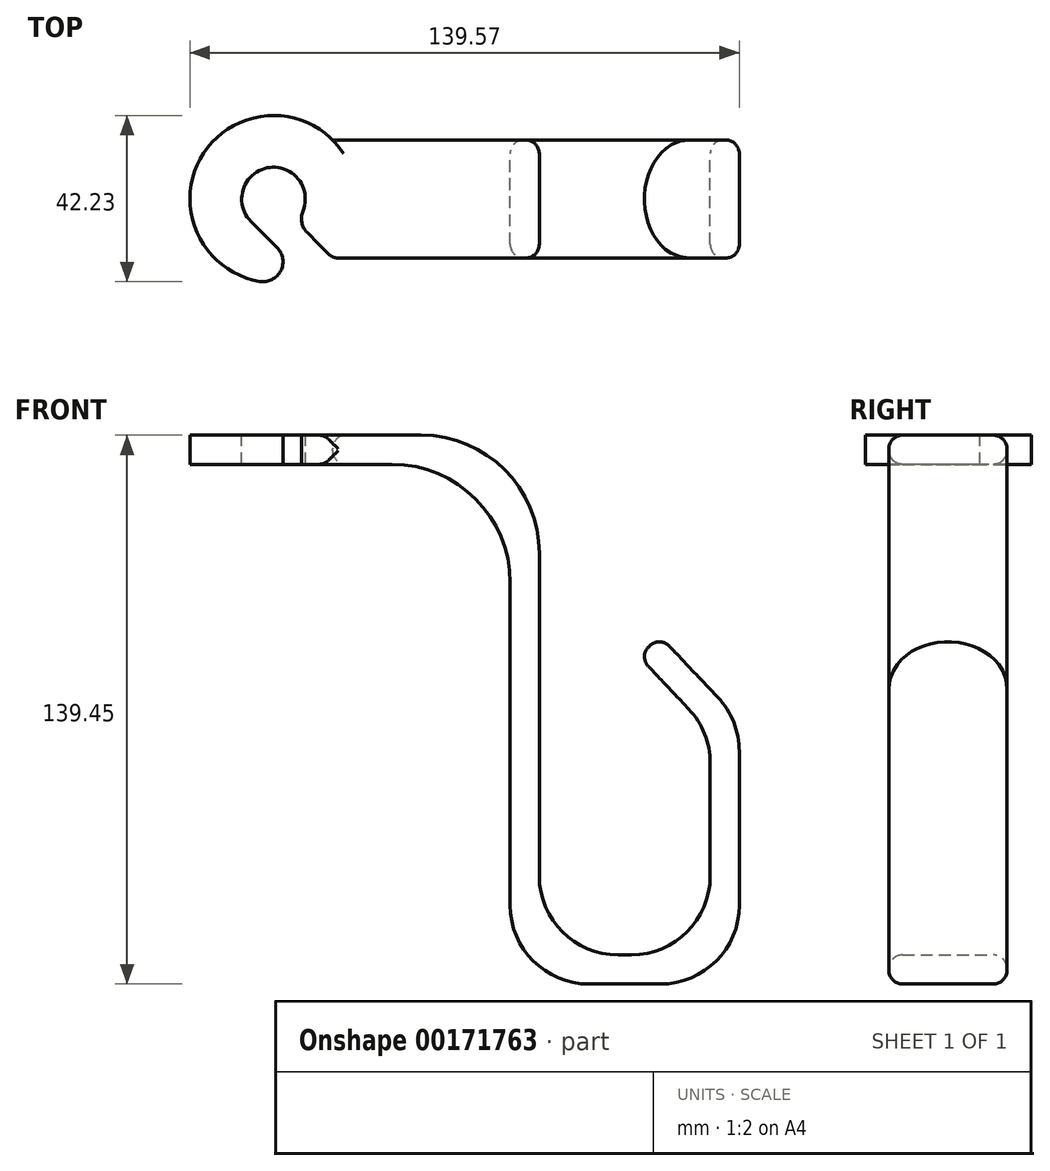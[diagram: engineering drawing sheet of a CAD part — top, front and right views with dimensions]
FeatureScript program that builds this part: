
annotation { "Feature Type Name" : "Feature", "Feature Type Description" : "" }
export const myFeature = defineFeature(function(context is Context, id is Id, definition is map)
    precondition{}
    {
        {
            var Q0;
            Q0=qCreatedBy(makeId("Front.planeOp"),FACE);
            var sketch = newSketch(context, id + "F0", { "sketchPlane" : qUnion([Q0])});
            skLineSegment(sketch, "E0", {"start": v(-48.01, 40.05) * mm, "end": v(34.52, 40.05) * mm});
            skLineSegment(sketch, "E1", {"start": v(34.52, 40.05) * mm, "end": v(34.52, -92) * mm});
            skLineSegment(sketch, "E2", {"start": v(34.52, -92) * mm, "end": v(77.93, -92) * mm});
            skLineSegment(sketch, "E3", {"start": v(77.93, -92) * mm, "end": v(77.93, -35.29) * mm});
            skLineSegment(sketch, "E4", {"start": v(77.93, -35.29) * mm, "end": v(59.78, -16.1) * mm});
            skLineSegment(sketch, "E5.0", {"start": v(85.33, -32.34) * mm, "end": v(65.16, -11.02) * mm});
            skLineSegment(sketch, "E5.1", {"start": v(-48.01, 32.65) * mm, "end": v(27.12, 32.65) * mm});
            skLineSegment(sketch, "E5.2", {"start": v(27.12, 32.65) * mm, "end": v(27.12, -99.4) * mm});
            skLineSegment(sketch, "E5.3", {"start": v(27.12, -99.4) * mm, "end": v(85.33, -99.4) * mm});
            skLineSegment(sketch, "E5.4", {"start": v(85.33, -99.4) * mm, "end": v(85.33, -32.34) * mm});
            skLineSegment(sketch, "E6", {"start": v(-48.01, 32.65) * mm, "end": v(-48.01, 40.05) * mm});
            skLineSegment(sketch, "E7", {"start": v(59.78, -16.1) * mm, "end": v(65.16, -11.02) * mm});
            skSolve(sketch);
        }
        {
            var Q0;
            Q0=makeQuery(id+"F0.imprint","IMPRINT",FACE,{"disambiguationData":[TD([[makeQuery(id+"F0.imprint","IMPRINT",EDGE,{"derivedFrom":sQuery(id+"F0.wireOp",EDGE,"E0")}),-1.0]])]});
            extrude(context, id + "F1", {"entities" : qUnion([Q0]), "endBound" : BoundingType.SYMMETRIC, "depth" : 30 * mm});
        }
        {
            var Q0;
            Q0=makeQuery(id+"F1.opExtrude","SWEPT_FACE",FACE,{"disambiguationData":[OSD([sQuery(id+"F0.wireOp",EDGE,"E0")])]});
            var sketch = newSketch(context, id + "F2", { "sketchPlane" : qUnion([Q0])});
            skLineSegment(sketch, "E8", {"start": v(-48.01, 15) * mm, "end": v(-48.01, -15) * mm});
            skLineSegment(sketch, "E9", {"start": v(-48.01, -15) * mm, "end": v(-18.01, -15) * mm});
            skLineSegment(sketch, "E10", {"start": v(-48.01, 15) * mm, "end": v(-18.01, -15) * mm});
            skCircle(sketch, "E11", {"center": v(-33.01, 0) * mm, "radius": 21.23 * mm});
            skCircle(sketch, "E12", {"center": v(-33.01, 0) * mm, "radius": 8.08 * mm});
            skLineSegment(sketch, "E13", {"start": v(-48.01, -15) * mm, "end": v(-33.01, 0) * mm});
            skLineSegment(sketch, "E14", {"start": v(-38.72, -5.71) * mm, "end": v(-29.44, -15) * mm});
            skLineSegment(sketch, "E15", {"start": v(-38.72, -5.71) * mm, "end": v(-24.85, -19.6) * mm});
            skSolve(sketch);
        }
        {
            var Q0;
            {var subQ4=sQuery(id+"F0.wireOp",EDGE,"E0");var subQ7=sQuery(id+"F2.wireOp",EDGE,"E11");var subQ8=makeQuery(id+"F1.opExtrude","CAP_EDGE",EDGE,{"disambiguationData":[OSD([subQ4])],"isStart":true});var subQ9=makeQuery(id+"F2.imprint","INTERSECT",VERTEX,{"derivedFrom":[subQ8,subQ7]});Q0=makeQuery(id+"F2.imprint","IMPRINT",FACE,{"disambiguationData":[TD([[makeQuery(id+"F2.imprint","IMPRINT",EDGE,{"disambiguationData":[TD([[subQ9,1.0]])],"derivedFrom":subQ7}),1.0]])]});}
            var Q1;
            {var subQ0=sQuery(id+"F2.wireOp",EDGE,"E8");Q1=makeQuery(id+"F2.imprint","IMPRINT",FACE,{"disambiguationData":[TD([[makeQuery(id+"F2.imprint","IMPRINT",EDGE,{"derivedFrom":subQ0}),-1.0]])]});}
            var Q2;
            {var subQ7=sQuery(id+"F2.wireOp",EDGE,"E8");Q2=makeQuery(id+"F2.imprint","IMPRINT",FACE,{"disambiguationData":[TD([[makeQuery(id+"F2.imprint","IMPRINT",EDGE,{"derivedFrom":subQ7}),1.0]])]});}
            var Q3;
            {var subQ1=sQuery(id+"F2.wireOp",EDGE,"E9");var subQ3=sQuery(id+"F2.wireOp",EDGE,"E15");var subQ4=makeQuery(id+"F2.imprint","INTERSECT",VERTEX,{"derivedFrom":[subQ1,subQ3]});Q3=makeQuery(id+"F2.imprint","IMPRINT",FACE,{"disambiguationData":[TD([[makeQuery(id+"F2.imprint","IMPRINT",EDGE,{"disambiguationData":[TD([[subQ4,1.0]])],"derivedFrom":subQ1}),1.0]])]});}
            extrude(context, id + "F3", {"entities" : qUnion([Q0, Q1, Q2, Q3]), "operationType" : NewBodyOperationType.ADD, "oppositeDirection" : true, "depth" : 7.4 * mm});
        }
        {
            var Q0;
            {var subQ0=sQuery(id+"F2.wireOp",EDGE,"E13");var subQ1=sQuery(id+"F2.wireOp",EDGE,"E10");var subQ2=makeQuery(id+"F2.imprint","INTERSECT",VERTEX,{"derivedFrom":[subQ1,subQ0]});Q0=makeQuery(id+"F2.imprint","IMPRINT",FACE,{"disambiguationData":[TD([[makeQuery(id+"F2.imprint","IMPRINT",EDGE,{"disambiguationData":[TD([[subQ2,-1.0]])],"derivedFrom":subQ1}),-1.0]])]});}
            var Q1;
            {var subQ0=sQuery(id+"F2.wireOp",EDGE,"E10");var subQ1=makeQuery(id+"F2.imprint","INTERSECT",VERTEX,{"derivedFrom":[subQ0,sQuery(id+"F2.wireOp",EDGE,"E13")]});Q1=makeQuery(id+"F2.imprint","IMPRINT",FACE,{"disambiguationData":[TD([[makeQuery(id+"F2.imprint","IMPRINT",EDGE,{"disambiguationData":[TD([[subQ1,1.0]])],"derivedFrom":subQ0}),1.0]])]});}
            var Q2;
            {var subQ0=sQuery(id+"F2.wireOp",EDGE,"E13");var subQ1=sQuery(id+"F2.wireOp",EDGE,"E10");var subQ2=makeQuery(id+"F2.imprint","INTERSECT",VERTEX,{"derivedFrom":[subQ1,subQ0]});Q2=makeQuery(id+"F2.imprint","IMPRINT",FACE,{"disambiguationData":[TD([[makeQuery(id+"F2.imprint","IMPRINT",EDGE,{"disambiguationData":[TD([[subQ2,1.0]])],"derivedFrom":subQ1}),-1.0]])]});}
            var Q3;
            {var subQ1=sQuery(id+"F2.wireOp",EDGE,"E9");var subQ3=sQuery(id+"F2.wireOp",EDGE,"E15");var subQ4=makeQuery(id+"F2.imprint","INTERSECT",VERTEX,{"derivedFrom":[subQ1,subQ3]});Q3=makeQuery(id+"F2.imprint","IMPRINT",FACE,{"disambiguationData":[TD([[makeQuery(id+"F2.imprint","IMPRINT",EDGE,{"disambiguationData":[TD([[subQ4,-1.0]])],"derivedFrom":subQ1}),1.0]])]});}
            extrude(context, id + "F4", {"entities" : qUnion([Q0, Q1, Q2, Q3]), "operationType" : NewBodyOperationType.REMOVE, "oppositeDirection" : true, "depth" : 25.4 * mm});
        }
        {
            var Q0;
            Q0=makeQuery(id+"F1.opExtrude","SWEPT_EDGE",EDGE,{"disambiguationData":[OSD([sQuery(id+"F0.wireOp",EDGE,"E0"),sQuery(id+"F0.wireOp",EDGE,"E1")])]});
            var Q1;
            Q1=makeQuery(id+"F1.opExtrude","SWEPT_EDGE",EDGE,{"disambiguationData":[OSD([sQuery(id+"F0.wireOp",EDGE,"E5.1"),sQuery(id+"F0.wireOp",EDGE,"E5.2")])]});
            fillet(context, id + "F5", {"entities" : qUnion([Q0, Q1]), "radius" : 30 * mm, "tangentPropagation" : true, "allowEdgeOverflow" : false});
        }
        {
            var Q0;
            Q0=makeQuery(id+"F1.opExtrude","SWEPT_EDGE",EDGE,{"disambiguationData":[OSD([sQuery(id+"F0.wireOp",EDGE,"E5.2"),sQuery(id+"F0.wireOp",EDGE,"E5.3")])]});
            var Q1;
            Q1=makeQuery(id+"F1.opExtrude","SWEPT_EDGE",EDGE,{"disambiguationData":[OSD([sQuery(id+"F0.wireOp",EDGE,"E1"),sQuery(id+"F0.wireOp",EDGE,"E2")])]});
            var Q2;
            Q2=makeQuery(id+"F1.opExtrude","SWEPT_EDGE",EDGE,{"disambiguationData":[OSD([sQuery(id+"F0.wireOp",EDGE,"E5.3"),sQuery(id+"F0.wireOp",EDGE,"E5.4")])]});
            var Q3;
            Q3=makeQuery(id+"F1.opExtrude","SWEPT_EDGE",EDGE,{"disambiguationData":[OSD([sQuery(id+"F0.wireOp",EDGE,"E2"),sQuery(id+"F0.wireOp",EDGE,"E3")])]});
            var Q4;
            Q4=makeQuery(id+"F1.opExtrude","SWEPT_EDGE",EDGE,{"disambiguationData":[OSD([sQuery(id+"F0.wireOp",EDGE,"E3"),sQuery(id+"F0.wireOp",EDGE,"E4")])]});
            var Q5;
            Q5=makeQuery(id+"F1.opExtrude","SWEPT_EDGE",EDGE,{"disambiguationData":[OSD([sQuery(id+"F0.wireOp",EDGE,"E5.0"),sQuery(id+"F0.wireOp",EDGE,"E5.4")])]});
            fillet(context, id + "F6", {"entities" : qUnion([Q0, Q1, Q2, Q3, Q4, Q5]), "radius" : 20 * mm, "tangentPropagation" : true, "allowEdgeOverflow" : false});
        }
        {
            var Q0;
            Q0=makeQuery(id+"F1.opExtrude","CAP_EDGE",EDGE,{"disambiguationData":[OSD([sQuery(id+"F0.wireOp",EDGE,"E7")])],"isStart":false});
            var Q1;
            Q1=makeQuery(id+"F1.opExtrude","CAP_EDGE",EDGE,{"disambiguationData":[OSD([sQuery(id+"F0.wireOp",EDGE,"E7")])],"isStart":true});
            fillet(context, id + "F7", {"entities" : qUnion([Q0, Q1]), "radius" : 15 * mm, "tangentPropagation" : true, "allowEdgeOverflow" : false});
        }
        {
            var Q0;
            Q0=makeQuery(id+"F3.opExtrude","SWEPT_EDGE",EDGE,{"disambiguationData":[OSD([sQuery(id+"F2.wireOp",EDGE,"E11"),sQuery(id+"F2.wireOp",EDGE,"E15")])]});
            var Q1;
            Q1=makeQuery(id+"F4.boolean.opBoolean","COPY",EDGE,{"derivedFrom":makeQuery(id+"F4.opExtrude","SWEPT_EDGE",EDGE,{"disambiguationData":[OSD([sQuery(id+"F2.wireOp",EDGE,"E10"),sQuery(id+"F2.wireOp",EDGE,"E12")])]})});
            var Q2;
            Q2=makeQuery(id+"F4.boolean.opBoolean","COPY",EDGE,{"derivedFrom":makeQuery(id+"F4.opExtrude","SWEPT_EDGE",EDGE,{"disambiguationData":[OSD([sQuery(id+"F0.wireOp",EDGE,"E0"),sQuery(id+"F2.wireOp",EDGE,"E9"),sQuery(id+"F2.wireOp",EDGE,"E10")])]})});
            fillet(context, id + "F8", {"entities" : qUnion([Q0, Q1, Q2]), "radius" : 5.08 * mm, "tangentPropagation" : true, "allowEdgeOverflow" : false});
        }
        {
            var Q0;
            Q0=makeQuery(id+"F1.opExtrude","CAP_FACE",FACE,{"disambiguationData":[OSD([sQuery(id+"F0.wireOp",EDGE,"E0"),sQuery(id+"F0.wireOp",EDGE,"E1"),sQuery(id+"F0.wireOp",EDGE,"E2"),sQuery(id+"F0.wireOp",EDGE,"E3"),sQuery(id+"F0.wireOp",EDGE,"E4"),sQuery(id+"F0.wireOp",EDGE,"E5.0"),sQuery(id+"F0.wireOp",EDGE,"E5.1"),sQuery(id+"F0.wireOp",EDGE,"E5.2"),sQuery(id+"F0.wireOp",EDGE,"E5.3"),sQuery(id+"F0.wireOp",EDGE,"E5.4"),sQuery(id+"F0.wireOp",EDGE,"E6"),sQuery(id+"F0.wireOp",EDGE,"E7")])],"isStart":false});
            fillet(context, id + "F9", {"entities" : qUnion([Q0]), "radius" : 3.5 * mm, "tangentPropagation" : true, "allowEdgeOverflow" : false});
        }
    });
